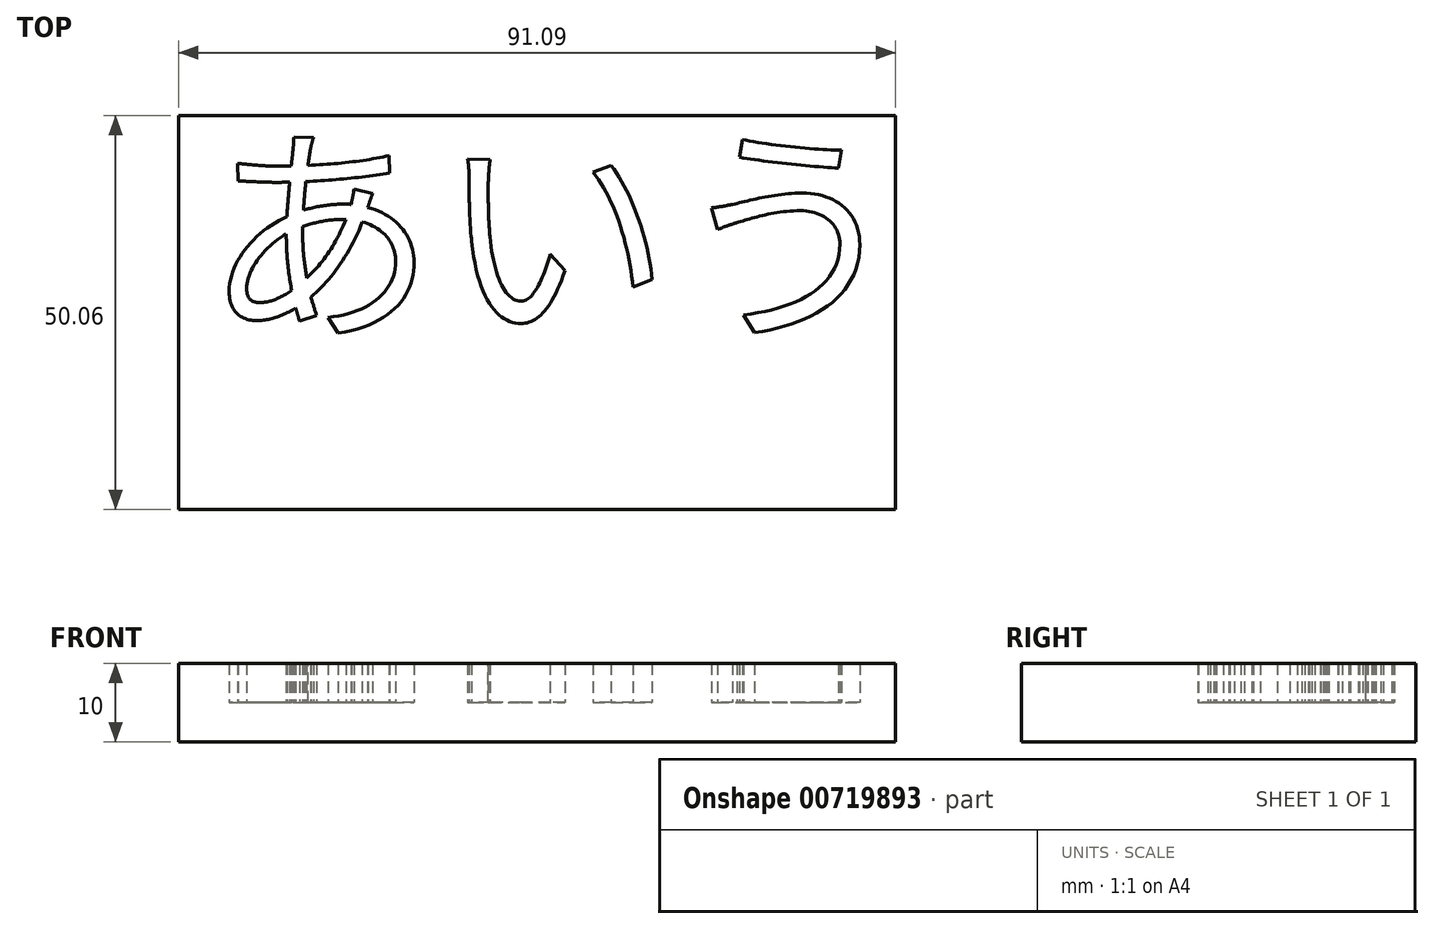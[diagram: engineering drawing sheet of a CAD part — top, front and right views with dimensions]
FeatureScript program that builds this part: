
annotation { "Feature Type Name" : "Feature", "Feature Type Description" : "" }
export const myFeature = defineFeature(function(context is Context, id is Id, definition is map)
    precondition{}
    {
        {
            var Q0;
            Q0=qCreatedBy(makeId("Top.planeOp"),FACE);
            var sketch = newSketch(context, id + "F0", { "sketchPlane" : qUnion([Q0])});
            skLineSegment(sketch, "E0.bottom", {"start": v(-42.31, 24.69) * mm, "end": v(48.78, 24.69) * mm});
            skLineSegment(sketch, "E0.top", {"start": v(-42.31, -25.37) * mm, "end": v(48.78, -25.37) * mm});
            skLineSegment(sketch, "E0.left", {"start": v(-42.31, 24.69) * mm, "end": v(-42.31, -25.37) * mm});
            skLineSegment(sketch, "E0.right", {"start": v(48.78, 24.69) * mm, "end": v(48.78, -25.37) * mm});
            skSolve(sketch);
        }
        {
            var Q0;
            Q0 = qSketchRegion(id + "F0", true);
            extrude(context, id + "F1", {"entities" : qUnion([Q0]), "depth" : 10 * mm, "offsetDistance" : 25 * mm});
        }
        {
            var Q0;
            Q0=qCreatedBy(makeId("Top.planeOp"),FACE);
            var sketch = newSketch(context, id + "F2", { "sketchPlane" : qUnion([Q0])});
            skText(sketch, "E1", { "text": "あいう", "fontName": "NotoSansCJKjp-Regular.otf"});
            const initialGuessF2  = {"E1": [-0.03925, -0.0516, 1, 0, 0.02145]};
            skSetInitialGuess(sketch, initialGuessF2);
            skSolve(sketch);
        }
        {
            var Q0;
            Q0 = qSketchRegion(id + "F2", true);
            extrude(context, id + "F3", {"entities" : qUnion([Q0]), "depth" : 5 * mm, "offsetDistance" : 25 * mm});
        }
        {
            var Q0;
            Q0=makeQuery(id+"F3.opExtrude","SWEPT_BODY",BODY,{"disambiguationData":[OSD([sQuery(id+"F2.wireOp",EDGE,"E1.sketch_text.stroke-0"),sQuery(id+"F2.wireOp",EDGE,"E1.sketch_text.stroke-1"),sQuery(id+"F2.wireOp",EDGE,"E1.sketch_text.stroke-2"),sQuery(id+"F2.wireOp",EDGE,"E1.sketch_text.stroke-3"),sQuery(id+"F2.wireOp",EDGE,"E1.sketch_text.stroke-4"),sQuery(id+"F2.wireOp",EDGE,"E1.sketch_text.stroke-5"),sQuery(id+"F2.wireOp",EDGE,"E1.sketch_text.stroke-6"),sQuery(id+"F2.wireOp",EDGE,"E1.sketch_text.stroke-7"),sQuery(id+"F2.wireOp",EDGE,"E1.sketch_text.stroke-8"),sQuery(id+"F2.wireOp",EDGE,"E1.sketch_text.stroke-9"),sQuery(id+"F2.wireOp",EDGE,"E1.sketch_text.stroke-10"),sQuery(id+"F2.wireOp",EDGE,"E1.sketch_text.stroke-11"),sQuery(id+"F2.wireOp",EDGE,"E1.sketch_text.stroke-12"),sQuery(id+"F2.wireOp",EDGE,"E1.sketch_text.stroke-13"),sQuery(id+"F2.wireOp",EDGE,"E1.sketch_text.stroke-14"),sQuery(id+"F2.wireOp",EDGE,"E1.sketch_text.stroke-15"),sQuery(id+"F2.wireOp",EDGE,"E1.sketch_text.stroke-16"),sQuery(id+"F2.wireOp",EDGE,"E1.sketch_text.stroke-17"),sQuery(id+"F2.wireOp",EDGE,"E1.sketch_text.stroke-18"),sQuery(id+"F2.wireOp",EDGE,"E1.sketch_text.stroke-19"),sQuery(id+"F2.wireOp",EDGE,"E1.sketch_text.stroke-20"),sQuery(id+"F2.wireOp",EDGE,"E1.sketch_text.stroke-21"),sQuery(id+"F2.wireOp",EDGE,"E1.sketch_text.stroke-22"),sQuery(id+"F2.wireOp",EDGE,"E1.sketch_text.stroke-23"),sQuery(id+"F2.wireOp",EDGE,"E1.sketch_text.stroke-24"),sQuery(id+"F2.wireOp",EDGE,"E1.sketch_text.stroke-25"),sQuery(id+"F2.wireOp",EDGE,"E1.sketch_text.stroke-26"),sQuery(id+"F2.wireOp",EDGE,"E1.sketch_text.stroke-27"),sQuery(id+"F2.wireOp",EDGE,"E1.sketch_text.stroke-28"),sQuery(id+"F2.wireOp",EDGE,"E1.sketch_text.stroke-29"),sQuery(id+"F2.wireOp",EDGE,"E1.sketch_text.stroke-30"),sQuery(id+"F2.wireOp",EDGE,"E1.sketch_text.stroke-31"),sQuery(id+"F2.wireOp",EDGE,"E1.sketch_text.stroke-32"),sQuery(id+"F2.wireOp",EDGE,"E1.sketch_text.stroke-33"),sQuery(id+"F2.wireOp",EDGE,"E1.sketch_text.stroke-34"),sQuery(id+"F2.wireOp",EDGE,"E1.sketch_text.stroke-35"),sQuery(id+"F2.wireOp",EDGE,"E1.sketch_text.stroke-36"),sQuery(id+"F2.wireOp",EDGE,"E1.sketch_text.stroke-37"),sQuery(id+"F2.wireOp",EDGE,"E1.sketch_text.stroke-38"),sQuery(id+"F2.wireOp",EDGE,"E1.sketch_text.stroke-39"),sQuery(id+"F2.wireOp",EDGE,"E1.sketch_text.stroke-40"),sQuery(id+"F2.wireOp",EDGE,"E1.sketch_text.stroke-41"),sQuery(id+"F2.wireOp",EDGE,"E1.sketch_text.stroke-42"),sQuery(id+"F2.wireOp",EDGE,"E1.sketch_text.stroke-43")])]});
            var Q1;
            Q1=makeQuery(id+"F3.opExtrude","SWEPT_BODY",BODY,{"disambiguationData":[OSD([sQuery(id+"F2.wireOp",EDGE,"E1.sketch_text.stroke-44"),sQuery(id+"F2.wireOp",EDGE,"E1.sketch_text.stroke-45"),sQuery(id+"F2.wireOp",EDGE,"E1.sketch_text.stroke-46"),sQuery(id+"F2.wireOp",EDGE,"E1.sketch_text.stroke-47"),sQuery(id+"F2.wireOp",EDGE,"E1.sketch_text.stroke-48"),sQuery(id+"F2.wireOp",EDGE,"E1.sketch_text.stroke-49"),sQuery(id+"F2.wireOp",EDGE,"E1.sketch_text.stroke-50"),sQuery(id+"F2.wireOp",EDGE,"E1.sketch_text.stroke-51"),sQuery(id+"F2.wireOp",EDGE,"E1.sketch_text.stroke-52"),sQuery(id+"F2.wireOp",EDGE,"E1.sketch_text.stroke-53")])]});
            var Q2;
            Q2=makeQuery(id+"F3.opExtrude","SWEPT_BODY",BODY,{"disambiguationData":[OSD([sQuery(id+"F2.wireOp",EDGE,"E1.sketch_text.stroke-54"),sQuery(id+"F2.wireOp",EDGE,"E1.sketch_text.stroke-55"),sQuery(id+"F2.wireOp",EDGE,"E1.sketch_text.stroke-56"),sQuery(id+"F2.wireOp",EDGE,"E1.sketch_text.stroke-57")])]});
            var Q3;
            Q3=makeQuery(id+"F3.opExtrude","SWEPT_BODY",BODY,{"disambiguationData":[OSD([sQuery(id+"F2.wireOp",EDGE,"E1.sketch_text.stroke-58"),sQuery(id+"F2.wireOp",EDGE,"E1.sketch_text.stroke-59"),sQuery(id+"F2.wireOp",EDGE,"E1.sketch_text.stroke-60"),sQuery(id+"F2.wireOp",EDGE,"E1.sketch_text.stroke-61"),sQuery(id+"F2.wireOp",EDGE,"E1.sketch_text.stroke-62"),sQuery(id+"F2.wireOp",EDGE,"E1.sketch_text.stroke-63"),sQuery(id+"F2.wireOp",EDGE,"E1.sketch_text.stroke-64"),sQuery(id+"F2.wireOp",EDGE,"E1.sketch_text.stroke-65"),sQuery(id+"F2.wireOp",EDGE,"E1.sketch_text.stroke-66"),sQuery(id+"F2.wireOp",EDGE,"E1.sketch_text.stroke-67")])]});
            var Q4;
            Q4=makeQuery(id+"F3.opExtrude","SWEPT_BODY",BODY,{"disambiguationData":[OSD([sQuery(id+"F2.wireOp",EDGE,"E1.sketch_text.stroke-68"),sQuery(id+"F2.wireOp",EDGE,"E1.sketch_text.stroke-69"),sQuery(id+"F2.wireOp",EDGE,"E1.sketch_text.stroke-70"),sQuery(id+"F2.wireOp",EDGE,"E1.sketch_text.stroke-71")])]});
            transform(context, id + "F4", {"entities" : qUnion([Q0, Q1, Q2, Q3, Q4]), "transformType" : TransformType.TRANSLATION_3D, "dx" : 0 * mm, "dy" : 50 * mm, "dz" : 5 * mm, "makeCopy" : false});
        }
        {
            var Q0;
            Q0=makeQuery(id+"F3.opExtrude","SWEPT_BODY",BODY,{"disambiguationData":[OSD([sQuery(id+"F2.wireOp",EDGE,"E1.sketch_text.stroke-58"),sQuery(id+"F2.wireOp",EDGE,"E1.sketch_text.stroke-59"),sQuery(id+"F2.wireOp",EDGE,"E1.sketch_text.stroke-60"),sQuery(id+"F2.wireOp",EDGE,"E1.sketch_text.stroke-61"),sQuery(id+"F2.wireOp",EDGE,"E1.sketch_text.stroke-62"),sQuery(id+"F2.wireOp",EDGE,"E1.sketch_text.stroke-63"),sQuery(id+"F2.wireOp",EDGE,"E1.sketch_text.stroke-64"),sQuery(id+"F2.wireOp",EDGE,"E1.sketch_text.stroke-65"),sQuery(id+"F2.wireOp",EDGE,"E1.sketch_text.stroke-66"),sQuery(id+"F2.wireOp",EDGE,"E1.sketch_text.stroke-67")])]});
            var Q1;
            Q1=makeQuery(id+"F3.opExtrude","SWEPT_BODY",BODY,{"disambiguationData":[OSD([sQuery(id+"F2.wireOp",EDGE,"E1.sketch_text.stroke-68"),sQuery(id+"F2.wireOp",EDGE,"E1.sketch_text.stroke-69"),sQuery(id+"F2.wireOp",EDGE,"E1.sketch_text.stroke-70"),sQuery(id+"F2.wireOp",EDGE,"E1.sketch_text.stroke-71")])]});
            var Q2;
            Q2=makeQuery(id+"F3.opExtrude","SWEPT_BODY",BODY,{"disambiguationData":[OSD([sQuery(id+"F2.wireOp",EDGE,"E1.sketch_text.stroke-54"),sQuery(id+"F2.wireOp",EDGE,"E1.sketch_text.stroke-55"),sQuery(id+"F2.wireOp",EDGE,"E1.sketch_text.stroke-56"),sQuery(id+"F2.wireOp",EDGE,"E1.sketch_text.stroke-57")])]});
            var Q3;
            Q3=makeQuery(id+"F3.opExtrude","SWEPT_BODY",BODY,{"disambiguationData":[OSD([sQuery(id+"F2.wireOp",EDGE,"E1.sketch_text.stroke-44"),sQuery(id+"F2.wireOp",EDGE,"E1.sketch_text.stroke-45"),sQuery(id+"F2.wireOp",EDGE,"E1.sketch_text.stroke-46"),sQuery(id+"F2.wireOp",EDGE,"E1.sketch_text.stroke-47"),sQuery(id+"F2.wireOp",EDGE,"E1.sketch_text.stroke-48"),sQuery(id+"F2.wireOp",EDGE,"E1.sketch_text.stroke-49"),sQuery(id+"F2.wireOp",EDGE,"E1.sketch_text.stroke-50"),sQuery(id+"F2.wireOp",EDGE,"E1.sketch_text.stroke-51"),sQuery(id+"F2.wireOp",EDGE,"E1.sketch_text.stroke-52"),sQuery(id+"F2.wireOp",EDGE,"E1.sketch_text.stroke-53")])]});
            var Q4;
            Q4=makeQuery(id+"F3.opExtrude","SWEPT_BODY",BODY,{"disambiguationData":[OSD([sQuery(id+"F2.wireOp",EDGE,"E1.sketch_text.stroke-0"),sQuery(id+"F2.wireOp",EDGE,"E1.sketch_text.stroke-1"),sQuery(id+"F2.wireOp",EDGE,"E1.sketch_text.stroke-2"),sQuery(id+"F2.wireOp",EDGE,"E1.sketch_text.stroke-3"),sQuery(id+"F2.wireOp",EDGE,"E1.sketch_text.stroke-4"),sQuery(id+"F2.wireOp",EDGE,"E1.sketch_text.stroke-5"),sQuery(id+"F2.wireOp",EDGE,"E1.sketch_text.stroke-6"),sQuery(id+"F2.wireOp",EDGE,"E1.sketch_text.stroke-7"),sQuery(id+"F2.wireOp",EDGE,"E1.sketch_text.stroke-8"),sQuery(id+"F2.wireOp",EDGE,"E1.sketch_text.stroke-9"),sQuery(id+"F2.wireOp",EDGE,"E1.sketch_text.stroke-10"),sQuery(id+"F2.wireOp",EDGE,"E1.sketch_text.stroke-11"),sQuery(id+"F2.wireOp",EDGE,"E1.sketch_text.stroke-12"),sQuery(id+"F2.wireOp",EDGE,"E1.sketch_text.stroke-13"),sQuery(id+"F2.wireOp",EDGE,"E1.sketch_text.stroke-14"),sQuery(id+"F2.wireOp",EDGE,"E1.sketch_text.stroke-15"),sQuery(id+"F2.wireOp",EDGE,"E1.sketch_text.stroke-16"),sQuery(id+"F2.wireOp",EDGE,"E1.sketch_text.stroke-17"),sQuery(id+"F2.wireOp",EDGE,"E1.sketch_text.stroke-18"),sQuery(id+"F2.wireOp",EDGE,"E1.sketch_text.stroke-19"),sQuery(id+"F2.wireOp",EDGE,"E1.sketch_text.stroke-20"),sQuery(id+"F2.wireOp",EDGE,"E1.sketch_text.stroke-21"),sQuery(id+"F2.wireOp",EDGE,"E1.sketch_text.stroke-22"),sQuery(id+"F2.wireOp",EDGE,"E1.sketch_text.stroke-23"),sQuery(id+"F2.wireOp",EDGE,"E1.sketch_text.stroke-24"),sQuery(id+"F2.wireOp",EDGE,"E1.sketch_text.stroke-25"),sQuery(id+"F2.wireOp",EDGE,"E1.sketch_text.stroke-26"),sQuery(id+"F2.wireOp",EDGE,"E1.sketch_text.stroke-27"),sQuery(id+"F2.wireOp",EDGE,"E1.sketch_text.stroke-28"),sQuery(id+"F2.wireOp",EDGE,"E1.sketch_text.stroke-29"),sQuery(id+"F2.wireOp",EDGE,"E1.sketch_text.stroke-30"),sQuery(id+"F2.wireOp",EDGE,"E1.sketch_text.stroke-31"),sQuery(id+"F2.wireOp",EDGE,"E1.sketch_text.stroke-32"),sQuery(id+"F2.wireOp",EDGE,"E1.sketch_text.stroke-33"),sQuery(id+"F2.wireOp",EDGE,"E1.sketch_text.stroke-34"),sQuery(id+"F2.wireOp",EDGE,"E1.sketch_text.stroke-35"),sQuery(id+"F2.wireOp",EDGE,"E1.sketch_text.stroke-36"),sQuery(id+"F2.wireOp",EDGE,"E1.sketch_text.stroke-37"),sQuery(id+"F2.wireOp",EDGE,"E1.sketch_text.stroke-38"),sQuery(id+"F2.wireOp",EDGE,"E1.sketch_text.stroke-39"),sQuery(id+"F2.wireOp",EDGE,"E1.sketch_text.stroke-40"),sQuery(id+"F2.wireOp",EDGE,"E1.sketch_text.stroke-41"),sQuery(id+"F2.wireOp",EDGE,"E1.sketch_text.stroke-42"),sQuery(id+"F2.wireOp",EDGE,"E1.sketch_text.stroke-43")])]});
            var Q5;
            Q5=makeQuery(id+"F1.opExtrude","SWEPT_BODY",BODY,{"disambiguationData":[OSD([sQuery(id+"F0.wireOp",EDGE,"E0.bottom"),sQuery(id+"F0.wireOp",EDGE,"E0.top"),sQuery(id+"F0.wireOp",EDGE,"E0.left"),sQuery(id+"F0.wireOp",EDGE,"E0.right")])]});
            booleanBodies(context, id + "F5", {"operationType" : BooleanOperationType.SUBTRACTION, "tools" : qUnion([Q0, Q1, Q2, Q3, Q4]), "targets" : qUnion([Q5])});
        }
    });
